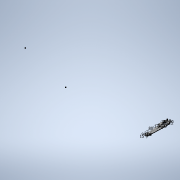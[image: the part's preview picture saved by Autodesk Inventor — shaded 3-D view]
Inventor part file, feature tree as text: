
AUTODESK INVENTOR PART (.ipt)
format: ipt  version: 2020.3 (Build 243373000, 373)  size: 190,464 bytes
history: native  units: mm
features: fillet x3, sketch x1, extrude x1, chamfer x1
ambient origin geometry x8: Origin, YZ Plane, XZ Plane, XY Plane, X Axis, Y Axis, Z Axis, Center Point
bodies: Solid1 (feature_tree)
feature tree (6):
  sketch  "Sketch1"  dims[d4=5.0mm d5=23.0mm d6=13.0mm d7=5.0mm d15=7.0mm d17=5.0mm d18=4.0mm d21=20.0mm d23=80.0mm d24=15.0mm d29=29.670597mm d30=6.0mm d31=10.0mm d33=5.0mm d34=0.0mm d37=2.5mm d38=2.0mm d39=45.0deg d40=3.0mm d41=3.0mm d42=2.0mm d43=4.0mm d44=3.0mm d45=4.0mm d50=13.0mm d51=12.0mm d52=22.68928mm d53=90.0deg]
  extrude  "Extrusion1"  Depth=23.0mm
  chamfer  "Chamfer1"  Distance=13.0mm
  fillet  "Fillet1"  Radius=5.0mm
  fillet  "Fillet2"  Radius=7.0mm
  fillet  "Fillet3"  Radius=5.0mm
